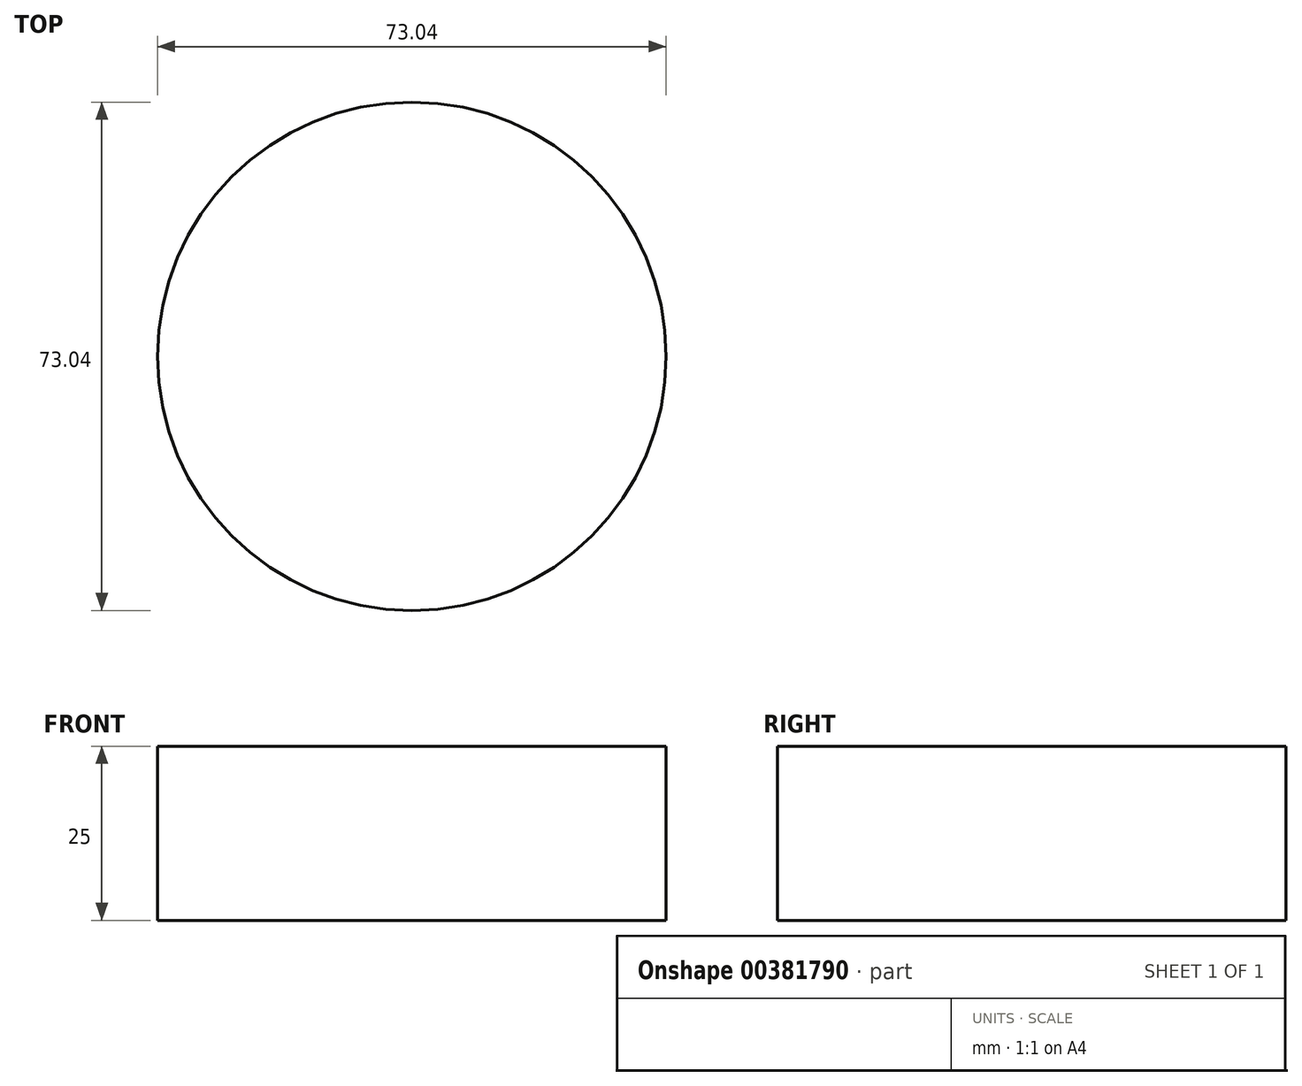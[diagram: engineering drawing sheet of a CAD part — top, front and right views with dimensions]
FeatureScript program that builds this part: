
annotation { "Feature Type Name" : "Feature", "Feature Type Description" : "" }
export const myFeature = defineFeature(function(context is Context, id is Id, definition is map)
    precondition{}
    {
        {
            var Q0;
            Q0=qCreatedBy(makeId("Top.planeOp"),FACE);
            var sketch = newSketch(context, id + "F0", { "sketchPlane" : qUnion([Q0])});
            skCircle(sketch, "E0", {"center": v(0, 0) * mm, "radius": 36.52 * mm});
            skSolve(sketch);
        }
        {
            var Q0;
            Q0=makeQuery(id+"F0.imprint","IMPRINT",FACE,{"disambiguationData":[TD([[makeQuery(id+"F0.imprint","IMPRINT",EDGE,{"derivedFrom":sQuery(id+"F0.wireOp",EDGE,"E0")}),1.0]])]});
            extrude(context, id + "F1", {"entities" : qUnion([Q0]), "depth" : 25 * mm});
        }
    });
